annotation { "Feature Type Name" : "Feature", "Feature Type Description" : "" }
export const myFeature = defineFeature(function(context is Context, id is Id, definition is map)
    precondition{}
    {
        {
            var Q0;
            Q0=qCreatedBy(makeId("Top.planeOp"),FACE);
            var sketch = newSketch(context, id + "F0", { "sketchPlane" : qUnion([Q0])});
            skLineSegment(sketch, "E0.bottom", {"start": v(-65, 37.5) * mm, "end": v(-10, 37.5) * mm});
            skLineSegment(sketch, "E0.top", {"start": v(-65, -37.5) * mm, "end": v(-10, -37.5) * mm});
            skLineSegment(sketch, "E0.left", {"start": v(-65, 37.5) * mm, "end": v(-65, -37.5) * mm});
            skLineSegment(sketch, "E0.right", {"start": v(65, 37.5) * mm, "end": v(65, -37.5) * mm});
            skLineSegment(sketch, "E1.bottom", {"start": v(7.7, 29) * mm, "end": v(8.3, 29) * mm});
            skLineSegment(sketch, "E1.top", {"start": v(7.7, -29) * mm, "end": v(8.3, -29) * mm});
            skLineSegment(sketch, "E1.left", {"start": v(7.7, 29) * mm, "end": v(7.7, -29) * mm});
            skLineSegment(sketch, "E1.right", {"start": v(8.3, 29) * mm, "end": v(8.3, -29) * mm});
            skLineSegment(sketch, "E2", {"start": v(8, 29) * mm, "end": v(8, -29) * mm, "construction": true});
            skLineSegment(sketch, "E3.bottom", {"start": v(-46.3, 29) * mm, "end": v(-45.7, 29) * mm});
            skLineSegment(sketch, "E3.top", {"start": v(-46.3, -29) * mm, "end": v(-45.7, -29) * mm});
            skLineSegment(sketch, "E3.left", {"start": v(-46.3, 29) * mm, "end": v(-46.3, -29) * mm});
            skLineSegment(sketch, "E3.right", {"start": v(-45.7, 29) * mm, "end": v(-45.7, -29) * mm});
            skLineSegment(sketch, "E4", {"start": v(-46, -29) * mm, "end": v(-46, 29) * mm, "construction": true});
            skLineSegment(sketch, "E5.bottom", {"start": v(-25, 10) * mm, "end": v(-13, 10) * mm});
            skLineSegment(sketch, "E5.top", {"start": v(-25, -10) * mm, "end": v(-13, -10) * mm});
            skLineSegment(sketch, "E5.left", {"start": v(-25, 10) * mm, "end": v(-25, -10) * mm});
            skLineSegment(sketch, "E5.right", {"start": v(-13, 10) * mm, "end": v(-13, -10) * mm});
            skLineSegment(sketch, "E6", {"start": v(-19, 10) * mm, "end": v(-19, -10) * mm, "construction": true});
            skLineSegment(sketch, "E7.bottom", {"start": v(-8, -35) * mm, "end": v(8, -35) * mm});
            skLineSegment(sketch, "E7.left", {"start": v(-10, -37) * mm, "end": v(-10, -37.5) * mm});
            skLineSegment(sketch, "E7.right", {"start": v(10, -37) * mm, "end": v(10, -37.5) * mm});
            skLineSegment(sketch, "E8.trimOffspring", {"start": v(10, -37.5) * mm, "end": v(65, -37.5) * mm});
            skLineSegment(sketch, "E9.top", {"start": v(-8, 35) * mm, "end": v(8, 35) * mm});
            skLineSegment(sketch, "E9.left", {"start": v(-10, 37.5) * mm, "end": v(-10, 37) * mm});
            skLineSegment(sketch, "E9.right", {"start": v(10, 37.5) * mm, "end": v(10, 37) * mm});
            skLineSegment(sketch, "E10.trimOffspring", {"start": v(10, 37.5) * mm, "end": v(65, 37.5) * mm});
            skPoint(sketch, "E11.visualSharp", {"position": v(-10, 35) * mm});
            skArc(sketch, "E11.filletArc", {"start": v(-10, 37) * mm, "mid": v(-9.41, 35.59) * mm, "end": v(-8, 35) * mm});
            skPoint(sketch, "E12.visualSharp", {"position": v(10, 35) * mm});
            skArc(sketch, "E12.filletArc", {"start": v(8, 35) * mm, "mid": v(9.41, 35.59) * mm, "end": v(10, 37) * mm});
            skPoint(sketch, "E13.visualSharp", {"position": v(-10, -35) * mm});
            skArc(sketch, "E13.filletArc", {"start": v(-8, -35) * mm, "mid": v(-9.41, -35.59) * mm, "end": v(-10, -37) * mm});
            skPoint(sketch, "E14.visualSharp", {"position": v(10, -35) * mm});
            skArc(sketch, "E14.filletArc", {"start": v(10, -37) * mm, "mid": v(9.41, -35.59) * mm, "end": v(8, -35) * mm});
            skSolve(sketch);
        }
        {
            var Q0;
            Q0 = qSketchRegion(id + "F0", true);
            extrude(context, id + "F1", {"entities" : qUnion([Q0]), "depth" : 4 * mm});
        }
        {
            var Q0;
            Q0=makeQuery(id+"F1.opExtrude","CAP_FACE",FACE,{"disambiguationData":[OSD([sQuery(id+"F0.wireOp",EDGE,"E0.bottom"),sQuery(id+"F0.wireOp",EDGE,"E0.top"),sQuery(id+"F0.wireOp",EDGE,"E0.left"),sQuery(id+"F0.wireOp",EDGE,"E0.right"),sQuery(id+"F0.wireOp",EDGE,"E1.bottom"),sQuery(id+"F0.wireOp",EDGE,"E1.top"),sQuery(id+"F0.wireOp",EDGE,"E1.left"),sQuery(id+"F0.wireOp",EDGE,"E1.right"),sQuery(id+"F0.wireOp",EDGE,"E3.bottom"),sQuery(id+"F0.wireOp",EDGE,"E3.top"),sQuery(id+"F0.wireOp",EDGE,"E3.left"),sQuery(id+"F0.wireOp",EDGE,"E3.right")])],"isStart":false});
            var sketch = newSketch(context, id + "F2", { "sketchPlane" : qUnion([Q0])});
            skCircle(sketch, "E15", {"center": v(-35, 11.75) * mm, "radius": 2.5 * mm});
            skCircle(sketch, "E16", {"center": v(-1, 11.75) * mm, "radius": 2.5 * mm});
            skCircle(sketch, "E17", {"center": v(17, 11.75) * mm, "radius": 2.5 * mm});
            skCircle(sketch, "E18", {"center": v(51, 11.75) * mm, "radius": 2.5 * mm});
            skLineSegment(sketch, "E19", {"start": v(8, 29) * mm, "end": v(8, 11.1) * mm, "construction": true});
            skCircle(sketch, "E20.MirrorC", {"center": v(-35, -11.75) * mm, "radius": 2.5 * mm});
            skCircle(sketch, "E21.MirrorC", {"center": v(-1, -11.75) * mm, "radius": 2.5 * mm});
            skCircle(sketch, "E22.MirrorC", {"center": v(17, -11.75) * mm, "radius": 2.5 * mm});
            skCircle(sketch, "E23.MirrorC", {"center": v(51, -11.75) * mm, "radius": 2.5 * mm});
            skLineSegment(sketch, "E24.bottom", {"start": v(65, 37.5) * mm, "end": v(62, 37.5) * mm});
            skLineSegment(sketch, "E24.top", {"start": v(65, -37.5) * mm, "end": v(62, -37.5) * mm});
            skLineSegment(sketch, "E24.left", {"start": v(65, 37.5) * mm, "end": v(65, -37.5) * mm});
            skLineSegment(sketch, "E24.right", {"start": v(62, 37.5) * mm, "end": v(62, -37.5) * mm});
            skSolve(sketch);
        }
        {
            var Q0;
            Q0 = qSketchRegion(id + "F2", true);
            extrude(context, id + "F3", {"entities" : qUnion([Q0]), "operationType" : NewBodyOperationType.ADD, "depth" : 6 * mm});
        }
        {
            var Q0;
            Q0=makeQuery(id+"F1.opExtrude","CAP_FACE",FACE,{"disambiguationData":[OSD([sQuery(id+"F0.wireOp",EDGE,"E0.bottom"),sQuery(id+"F0.wireOp",EDGE,"E0.top"),sQuery(id+"F0.wireOp",EDGE,"E0.left"),sQuery(id+"F0.wireOp",EDGE,"E0.right"),sQuery(id+"F0.wireOp",EDGE,"E1.bottom"),sQuery(id+"F0.wireOp",EDGE,"E1.top"),sQuery(id+"F0.wireOp",EDGE,"E1.left"),sQuery(id+"F0.wireOp",EDGE,"E1.right"),sQuery(id+"F0.wireOp",EDGE,"E3.bottom"),sQuery(id+"F0.wireOp",EDGE,"E3.top"),sQuery(id+"F0.wireOp",EDGE,"E3.left"),sQuery(id+"F0.wireOp",EDGE,"E3.right"),sQuery(id+"F0.wireOp",EDGE,"E5.bottom"),sQuery(id+"F0.wireOp",EDGE,"E5.top"),sQuery(id+"F0.wireOp",EDGE,"E5.left"),sQuery(id+"F0.wireOp",EDGE,"E5.right")])],"isStart":false});
            var sketch = newSketch(context, id + "F4", { "sketchPlane" : qUnion([Q0])});
            skLineSegment(sketch, "E25.bottom", {"start": v(-19.4, 10) * mm, "end": v(-18.6, 10) * mm});
            skLineSegment(sketch, "E25.top", {"start": v(-19.4, 15) * mm, "end": v(-18.6, 15) * mm});
            skLineSegment(sketch, "E25.left", {"start": v(-19.4, 10) * mm, "end": v(-19.4, 15) * mm});
            skLineSegment(sketch, "E25.right", {"start": v(-18.6, 10) * mm, "end": v(-18.6, 15) * mm});
            skLineSegment(sketch, "E26.bottom", {"start": v(-19.4, -10) * mm, "end": v(-18.6, -10) * mm});
            skLineSegment(sketch, "E26.top", {"start": v(-19.4, -15) * mm, "end": v(-18.6, -15) * mm});
            skLineSegment(sketch, "E26.left", {"start": v(-19.4, -10) * mm, "end": v(-19.4, -15) * mm});
            skLineSegment(sketch, "E26.right", {"start": v(-18.6, -10) * mm, "end": v(-18.6, -15) * mm});
            skLineSegment(sketch, "E27", {"start": v(-19, -10) * mm, "end": v(-19, 10) * mm, "construction": true});
            skSolve(sketch);
        }
        {
            var Q0;
            Q0 = qSketchRegion(id + "F4", true);
            extrude(context, id + "F5", {"entities" : qUnion([Q0]), "operationType" : NewBodyOperationType.REMOVE, "oppositeDirection" : true, "depth" : .6 * mm});
        }
        {
            var Q0;
            Q0=makeQuery(id+"F1.opExtrude","CAP_FACE",FACE,{"disambiguationData":[OSD([sQuery(id+"F0.wireOp",EDGE,"E0.bottom"),sQuery(id+"F0.wireOp",EDGE,"E0.top"),sQuery(id+"F0.wireOp",EDGE,"E0.left"),sQuery(id+"F0.wireOp",EDGE,"E0.right"),sQuery(id+"F0.wireOp",EDGE,"E1.bottom"),sQuery(id+"F0.wireOp",EDGE,"E1.top"),sQuery(id+"F0.wireOp",EDGE,"E1.left"),sQuery(id+"F0.wireOp",EDGE,"E1.right"),sQuery(id+"F0.wireOp",EDGE,"E3.bottom"),sQuery(id+"F0.wireOp",EDGE,"E3.top"),sQuery(id+"F0.wireOp",EDGE,"E3.left"),sQuery(id+"F0.wireOp",EDGE,"E3.right"),sQuery(id+"F0.wireOp",EDGE,"E5.bottom"),sQuery(id+"F0.wireOp",EDGE,"E5.top"),sQuery(id+"F0.wireOp",EDGE,"E5.left"),sQuery(id+"F0.wireOp",EDGE,"E5.right")])],"isStart":false});
            var sketch = newSketch(context, id + "F6", { "sketchPlane" : qUnion([Q0])});
            skLineSegment(sketch, "E28.bottom", {"start": v(-65, 37.5) * mm, "end": v(60.6, 37.5) * mm});
            skLineSegment(sketch, "E28.top", {"start": v(-65, -37.5) * mm, "end": v(60.6, -37.5) * mm});
            skLineSegment(sketch, "E28.left", {"start": v(-65, 37.5) * mm, "end": v(-65, -37.5) * mm});
            skLineSegment(sketch, "E28.right", {"start": v(60.6, 37.5) * mm, "end": v(60.6, -37.5) * mm});
            skCircle(sketch, "E29", {"center": v(-35, 11.75) * mm, "radius": 3 * mm});
            skCircle(sketch, "E30", {"center": v(-1, 11.75) * mm, "radius": 3 * mm});
            skCircle(sketch, "E31", {"center": v(17, 11.75) * mm, "radius": 3 * mm});
            skCircle(sketch, "E32", {"center": v(51, 11.75) * mm, "radius": 3 * mm});
            skCircle(sketch, "E33", {"center": v(-35, -11.75) * mm, "radius": 3 * mm});
            skCircle(sketch, "E34", {"center": v(-1, -11.75) * mm, "radius": 3 * mm});
            skCircle(sketch, "E35", {"center": v(17, -11.75) * mm, "radius": 3 * mm});
            skCircle(sketch, "E36", {"center": v(51, -11.75) * mm, "radius": 3 * mm});
            skLineSegment(sketch, "E37.bottom", {"start": v(-46, 29) * mm, "end": v(-46, 29) * mm});
            skLineSegment(sketch, "E37.top", {"start": v(-46, -29) * mm, "end": v(-46, -29) * mm});
            skLineSegment(sketch, "E37.left", {"start": v(-46.4, 28.6) * mm, "end": v(-46.4, -28.6) * mm});
            skLineSegment(sketch, "E37.right", {"start": v(-45.6, 28.6) * mm, "end": v(-45.6, -28.6) * mm});
            skLineSegment(sketch, "E38", {"start": v(-46, 29) * mm, "end": v(-46, 25.94) * mm, "construction": true});
            skLineSegment(sketch, "E39.bottom", {"start": v(8, 29) * mm, "end": v(8, 29) * mm});
            skLineSegment(sketch, "E39.top", {"start": v(8, -29) * mm, "end": v(8, -29) * mm});
            skLineSegment(sketch, "E39.left", {"start": v(7.6, 28.6) * mm, "end": v(7.6, -28.6) * mm});
            skLineSegment(sketch, "E39.right", {"start": v(8.4, 28.6) * mm, "end": v(8.4, -28.6) * mm});
            skLineSegment(sketch, "E40", {"start": v(8, 29) * mm, "end": v(8, 25.9) * mm, "construction": true});
            skLineSegment(sketch, "E41.bottom", {"start": v(-23, 15) * mm, "end": v(-15, 15) * mm});
            skLineSegment(sketch, "E41.top", {"start": v(-23, -15) * mm, "end": v(-15, -15) * mm});
            skLineSegment(sketch, "E41.left", {"start": v(-25, 13) * mm, "end": v(-25, -13) * mm});
            skLineSegment(sketch, "E41.right", {"start": v(-13, 13) * mm, "end": v(-13, -13) * mm});
            skPoint(sketch, "E42.visualSharp", {"position": v(-25, 15) * mm});
            skArc(sketch, "E42.filletArc", {"start": v(-23, 15) * mm, "mid": v(-24.41, 14.41) * mm, "end": v(-25, 13) * mm});
            skPoint(sketch, "E43.visualSharp", {"position": v(-13, 15) * mm});
            skArc(sketch, "E43.filletArc", {"start": v(-13, 13) * mm, "mid": v(-13.59, 14.41) * mm, "end": v(-15, 15) * mm});
            skPoint(sketch, "E44.visualSharp", {"position": v(-13, -15) * mm});
            skArc(sketch, "E44.filletArc", {"start": v(-15, -15) * mm, "mid": v(-13.59, -14.41) * mm, "end": v(-13, -13) * mm});
            skPoint(sketch, "E45.visualSharp", {"position": v(-25, -15) * mm});
            skArc(sketch, "E45.filletArc", {"start": v(-25, -13) * mm, "mid": v(-24.41, -14.41) * mm, "end": v(-23, -15) * mm});
            skPoint(sketch, "E46.visualSharp", {"position": v(-46.4, 29) * mm});
            skArc(sketch, "E46.filletArc", {"start": v(-46, 29) * mm, "mid": v(-46.28, 28.88) * mm, "end": v(-46.4, 28.6) * mm});
            skPoint(sketch, "E47.visualSharp", {"position": v(-45.6, 29) * mm});
            skArc(sketch, "E47.filletArc", {"start": v(-45.6, 28.6) * mm, "mid": v(-45.72, 28.88) * mm, "end": v(-46, 29) * mm});
            skPoint(sketch, "E48.visualSharp", {"position": v(-46.4, -29) * mm});
            skArc(sketch, "E48.filletArc", {"start": v(-46.4, -28.6) * mm, "mid": v(-46.28, -28.88) * mm, "end": v(-46, -29) * mm});
            skPoint(sketch, "E49.visualSharp", {"position": v(-45.6, -29) * mm});
            skArc(sketch, "E49.filletArc", {"start": v(-46, -29) * mm, "mid": v(-45.72, -28.88) * mm, "end": v(-45.6, -28.6) * mm});
            skPoint(sketch, "E50.visualSharp", {"position": v(7.6, 29) * mm});
            skArc(sketch, "E50.filletArc", {"start": v(8, 29) * mm, "mid": v(7.72, 28.88) * mm, "end": v(7.6, 28.6) * mm});
            skPoint(sketch, "E51.visualSharp", {"position": v(8.4, 29) * mm});
            skArc(sketch, "E51.filletArc", {"start": v(8.4, 28.6) * mm, "mid": v(8.28, 28.88) * mm, "end": v(8, 29) * mm});
            skPoint(sketch, "E52.visualSharp", {"position": v(7.6, -29) * mm});
            skArc(sketch, "E52.filletArc", {"start": v(7.6, -28.6) * mm, "mid": v(7.72, -28.88) * mm, "end": v(8, -29) * mm});
            skPoint(sketch, "E53.visualSharp", {"position": v(8.4, -29) * mm});
            skArc(sketch, "E53.filletArc", {"start": v(8, -29) * mm, "mid": v(8.28, -28.88) * mm, "end": v(8.4, -28.6) * mm});
            skSolve(sketch);
        }
        {
            var Q0;
            Q0 = qSketchRegion(id + "F6", true);
            extrude(context, id + "F7", {"entities" : qUnion([Q0]), "depth" : 4 * mm});
        }
        {
            var Q0;
            Q0=makeQuery(id+"F1.opExtrude","SWEPT_EDGE",EDGE,{"disambiguationData":[OSD([sQuery(id+"F0.wireOp",EDGE,"E5.bottom"),sQuery(id+"F0.wireOp",EDGE,"E5.left")])]});
            var Q1;
            Q1=makeQuery(id+"F1.opExtrude","SWEPT_EDGE",EDGE,{"disambiguationData":[OSD([sQuery(id+"F0.wireOp",EDGE,"E5.bottom"),sQuery(id+"F0.wireOp",EDGE,"E5.right")])]});
            var Q2;
            Q2=makeQuery(id+"F1.opExtrude","SWEPT_EDGE",EDGE,{"disambiguationData":[OSD([sQuery(id+"F0.wireOp",EDGE,"E5.top"),sQuery(id+"F0.wireOp",EDGE,"E5.right")])]});
            var Q3;
            Q3=makeQuery(id+"F1.opExtrude","SWEPT_EDGE",EDGE,{"disambiguationData":[OSD([sQuery(id+"F0.wireOp",EDGE,"E5.top"),sQuery(id+"F0.wireOp",EDGE,"E5.left")])]});
            fillet(context, id + "F8", {"entities" : qUnion([Q0, Q1, Q2, Q3]), "radius" : 2 * mm, "tangentPropagation" : true, "allowEdgeOverflow" : false});
        }
        {
            var Q0;
            Q0=makeQuery(id+"F3.opExtrude","CAP_EDGE",EDGE,{"disambiguationData":[OSD([sQuery(id+"F2.wireOp",EDGE,"E15")])],"isStart":false});
            var Q1;
            Q1=makeQuery(id+"F3.opExtrude","CAP_EDGE",EDGE,{"disambiguationData":[OSD([sQuery(id+"F2.wireOp",EDGE,"E20.MirrorC")])],"isStart":false});
            var Q2;
            Q2=makeQuery(id+"F3.opExtrude","CAP_EDGE",EDGE,{"disambiguationData":[OSD([sQuery(id+"F2.wireOp",EDGE,"E16")])],"isStart":false});
            var Q3;
            Q3=makeQuery(id+"F3.opExtrude","CAP_EDGE",EDGE,{"disambiguationData":[OSD([sQuery(id+"F2.wireOp",EDGE,"E21.MirrorC")])],"isStart":false});
            var Q4;
            Q4=makeQuery(id+"F3.opExtrude","CAP_EDGE",EDGE,{"disambiguationData":[OSD([sQuery(id+"F2.wireOp",EDGE,"E17")])],"isStart":false});
            var Q5;
            Q5=makeQuery(id+"F3.opExtrude","CAP_EDGE",EDGE,{"disambiguationData":[OSD([sQuery(id+"F2.wireOp",EDGE,"E22.MirrorC")])],"isStart":false});
            var Q6;
            Q6=makeQuery(id+"F3.opExtrude","CAP_EDGE",EDGE,{"disambiguationData":[OSD([sQuery(id+"F2.wireOp",EDGE,"E18")])],"isStart":false});
            var Q7;
            Q7=makeQuery(id+"F3.opExtrude","CAP_EDGE",EDGE,{"disambiguationData":[OSD([sQuery(id+"F2.wireOp",EDGE,"E23.MirrorC")])],"isStart":false});
            fillet(context, id + "F9", {"entities" : qUnion([Q0, Q1, Q2, Q3, Q4, Q5, Q6, Q7]), "radius" : 1 * mm, "tangentPropagation" : true, "allowEdgeOverflow" : false});
        }
        {
            var Q0;
            Q0=makeQuery(id+"F7.opExtrude","SWEPT_EDGE",EDGE,{"disambiguationData":[OSD([sQuery(id+"F0.wireOp",EDGE,"E8.trimOffspring"),sQuery(id+"F6.wireOp",EDGE,"E28.top"),sQuery(id+"F6.wireOp",EDGE,"E28.right")])]});
            var Q1;
            Q1=makeQuery(id+"F1.opExtrude","SWEPT_EDGE",EDGE,{"disambiguationData":[OSD([sQuery(id+"F0.wireOp",EDGE,"E0.top"),sQuery(id+"F0.wireOp",EDGE,"E0.left")])]});
            var Q2;
            Q2=makeQuery(id+"F1.opExtrude","SWEPT_EDGE",EDGE,{"disambiguationData":[OSD([sQuery(id+"F0.wireOp",EDGE,"E0.bottom"),sQuery(id+"F0.wireOp",EDGE,"E0.left")])]});
            var Q3;
            Q3=makeQuery(id+"F7.opExtrude","SWEPT_EDGE",EDGE,{"disambiguationData":[OSD([sQuery(id+"F6.wireOp",EDGE,"E28.bottom"),sQuery(id+"F6.wireOp",EDGE,"E28.left")])]});
            var Q4;
            Q4=makeQuery(id+"F7.opExtrude","SWEPT_EDGE",EDGE,{"disambiguationData":[OSD([sQuery(id+"F0.wireOp",EDGE,"E10.trimOffspring"),sQuery(id+"F6.wireOp",EDGE,"E28.bottom"),sQuery(id+"F6.wireOp",EDGE,"E28.right")])]});
            var Q5;
            Q5=makeQuery(id+"F7.opExtrude","SWEPT_EDGE",EDGE,{"disambiguationData":[OSD([sQuery(id+"F6.wireOp",EDGE,"E28.top"),sQuery(id+"F6.wireOp",EDGE,"E28.left")])]});
            var Q6;
            Q6=makeQuery(id+"F1.opExtrude","SWEPT_EDGE",EDGE,{"disambiguationData":[OSD([sQuery(id+"F0.wireOp",EDGE,"E0.top"),sQuery(id+"F0.wireOp",EDGE,"E7.left")])]});
            var Q7;
            Q7=makeQuery(id+"F1.opExtrude","SWEPT_EDGE",EDGE,{"disambiguationData":[OSD([sQuery(id+"F0.wireOp",EDGE,"E9.right"),sQuery(id+"F0.wireOp",EDGE,"E10.trimOffspring")])]});
            var Q8;
            Q8=makeQuery(id+"F1.opExtrude","SWEPT_EDGE",EDGE,{"disambiguationData":[OSD([sQuery(id+"F0.wireOp",EDGE,"E0.bottom"),sQuery(id+"F0.wireOp",EDGE,"E9.left")])]});
            var Q9;
            Q9=makeQuery(id+"F3.opExtrude","CAP_EDGE",EDGE,{"disambiguationData":[OSD([sQuery(id+"F2.wireOp",EDGE,"E24.bottom")])],"isStart":false});
            var Q10;
            Q10=makeQuery(id+"F3.opExtrude","CAP_EDGE",EDGE,{"disambiguationData":[OSD([sQuery(id+"F2.wireOp",EDGE,"E24.top")])],"isStart":false});
            var Q11;
            Q11=makeQuery(id+"F1.opExtrude","SWEPT_EDGE",EDGE,{"disambiguationData":[OSD([sQuery(id+"F0.wireOp",EDGE,"E7.right"),sQuery(id+"F0.wireOp",EDGE,"E8.trimOffspring")])]});
            fillet(context, id + "F10", {"entities" : qUnion([Q0, Q1, Q2, Q3, Q4, Q5, Q6, Q7, Q8, Q9, Q10, Q11]), "radius" : 5 * mm, "tangentPropagation" : true, "allowEdgeOverflow" : false});
        }
        {
            var Q0;
            Q0=makeQuery(id+"F1.opExtrude","CAP_FACE",FACE,{"disambiguationData":[OSD([sQuery(id+"F0.wireOp",EDGE,"E0.bottom"),sQuery(id+"F0.wireOp",EDGE,"E0.top"),sQuery(id+"F0.wireOp",EDGE,"E0.left"),sQuery(id+"F0.wireOp",EDGE,"E0.right"),sQuery(id+"F0.wireOp",EDGE,"E1.bottom"),sQuery(id+"F0.wireOp",EDGE,"E1.top"),sQuery(id+"F0.wireOp",EDGE,"E1.left"),sQuery(id+"F0.wireOp",EDGE,"E1.right"),sQuery(id+"F0.wireOp",EDGE,"E3.bottom"),sQuery(id+"F0.wireOp",EDGE,"E3.top"),sQuery(id+"F0.wireOp",EDGE,"E3.left"),sQuery(id+"F0.wireOp",EDGE,"E3.right"),sQuery(id+"F0.wireOp",EDGE,"E5.bottom"),sQuery(id+"F0.wireOp",EDGE,"E5.top"),sQuery(id+"F0.wireOp",EDGE,"E5.left"),sQuery(id+"F0.wireOp",EDGE,"E5.right"),sQuery(id+"F0.wireOp",EDGE,"E7.bottom"),sQuery(id+"F0.wireOp",EDGE,"E7.left"),sQuery(id+"F0.wireOp",EDGE,"E7.right"),sQuery(id+"F0.wireOp",EDGE,"E8.trimOffspring"),sQuery(id+"F0.wireOp",EDGE,"E9.top"),sQuery(id+"F0.wireOp",EDGE,"E9.left"),sQuery(id+"F0.wireOp",EDGE,"E9.right"),sQuery(id+"F0.wireOp",EDGE,"E10.trimOffspring"),sQuery(id+"F0.wireOp",EDGE,"E11.filletArc"),sQuery(id+"F0.wireOp",EDGE,"E12.filletArc"),sQuery(id+"F0.wireOp",EDGE,"E13.filletArc"),sQuery(id+"F0.wireOp",EDGE,"E14.filletArc")])],"isStart":true});
            fillet(context, id + "F11", {"entities" : qUnion([Q0]), "radius" : .75 * mm, "tangentPropagation" : true, "allowEdgeOverflow" : false});
        }
        {
            var Q0;
            Q0=makeQuery(id+"F7.opExtrude","CAP_FACE",FACE,{"disambiguationData":[OSD([sQuery(id+"F6.wireOp",EDGE,"E28.bottom"),sQuery(id+"F6.wireOp",EDGE,"E28.top"),sQuery(id+"F6.wireOp",EDGE,"E28.left"),sQuery(id+"F6.wireOp",EDGE,"E28.right"),sQuery(id+"F6.wireOp",EDGE,"E29"),sQuery(id+"F6.wireOp",EDGE,"E30"),sQuery(id+"F6.wireOp",EDGE,"E31"),sQuery(id+"F6.wireOp",EDGE,"E32"),sQuery(id+"F6.wireOp",EDGE,"E33"),sQuery(id+"F6.wireOp",EDGE,"E34"),sQuery(id+"F6.wireOp",EDGE,"E35"),sQuery(id+"F6.wireOp",EDGE,"E36"),sQuery(id+"F6.wireOp",EDGE,"E37.left"),sQuery(id+"F6.wireOp",EDGE,"E37.right"),sQuery(id+"F6.wireOp",EDGE,"E39.left"),sQuery(id+"F6.wireOp",EDGE,"E39.right"),sQuery(id+"F6.wireOp",EDGE,"E41.bottom"),sQuery(id+"F6.wireOp",EDGE,"E41.top"),sQuery(id+"F6.wireOp",EDGE,"E41.left"),sQuery(id+"F6.wireOp",EDGE,"E41.right"),sQuery(id+"F6.wireOp",EDGE,"E42.filletArc"),sQuery(id+"F6.wireOp",EDGE,"E43.filletArc"),sQuery(id+"F6.wireOp",EDGE,"E44.filletArc"),sQuery(id+"F6.wireOp",EDGE,"E45.filletArc"),sQuery(id+"F6.wireOp",EDGE,"E46.filletArc"),sQuery(id+"F6.wireOp",EDGE,"E47.filletArc"),sQuery(id+"F6.wireOp",EDGE,"E48.filletArc"),sQuery(id+"F6.wireOp",EDGE,"E49.filletArc"),sQuery(id+"F6.wireOp",EDGE,"E50.filletArc"),sQuery(id+"F6.wireOp",EDGE,"E51.filletArc"),sQuery(id+"F6.wireOp",EDGE,"E52.filletArc"),sQuery(id+"F6.wireOp",EDGE,"E53.filletArc")])],"isStart":true});
            fillet(context, id + "F12", {"entities" : qUnion([Q0]), "radius" : .75 * mm, "tangentPropagation" : true, "allowEdgeOverflow" : false});
        }
        {
            var Q0;
            Q0=makeQuery(id+"F1.opExtrude","CAP_FACE",FACE,{"disambiguationData":[OSD([sQuery(id+"F0.wireOp",EDGE,"E0.bottom"),sQuery(id+"F0.wireOp",EDGE,"E0.top"),sQuery(id+"F0.wireOp",EDGE,"E0.left"),sQuery(id+"F0.wireOp",EDGE,"E0.right"),sQuery(id+"F0.wireOp",EDGE,"E1.bottom"),sQuery(id+"F0.wireOp",EDGE,"E1.top"),sQuery(id+"F0.wireOp",EDGE,"E1.left"),sQuery(id+"F0.wireOp",EDGE,"E1.right"),sQuery(id+"F0.wireOp",EDGE,"E3.bottom"),sQuery(id+"F0.wireOp",EDGE,"E3.top"),sQuery(id+"F0.wireOp",EDGE,"E3.left"),sQuery(id+"F0.wireOp",EDGE,"E3.right"),sQuery(id+"F0.wireOp",EDGE,"E5.bottom"),sQuery(id+"F0.wireOp",EDGE,"E5.top"),sQuery(id+"F0.wireOp",EDGE,"E5.left"),sQuery(id+"F0.wireOp",EDGE,"E5.right"),sQuery(id+"F0.wireOp",EDGE,"E7.bottom"),sQuery(id+"F0.wireOp",EDGE,"E7.left"),sQuery(id+"F0.wireOp",EDGE,"E7.right"),sQuery(id+"F0.wireOp",EDGE,"E8.trimOffspring"),sQuery(id+"F0.wireOp",EDGE,"E9.top"),sQuery(id+"F0.wireOp",EDGE,"E9.left"),sQuery(id+"F0.wireOp",EDGE,"E9.right"),sQuery(id+"F0.wireOp",EDGE,"E10.trimOffspring"),sQuery(id+"F0.wireOp",EDGE,"E11.filletArc"),sQuery(id+"F0.wireOp",EDGE,"E12.filletArc"),sQuery(id+"F0.wireOp",EDGE,"E13.filletArc"),sQuery(id+"F0.wireOp",EDGE,"E14.filletArc")])],"isStart":false});
            var sketch = newSketch(context, id + "F13", { "sketchPlane" : qUnion([Q0])});
            skLineSegment(sketch, "E54.bottom", {"start": v(62, 13.94) * mm, "end": v(60, 13.94) * mm});
            skLineSegment(sketch, "E54.top", {"start": v(62, -13.94) * mm, "end": v(60, -13.94) * mm});
            skLineSegment(sketch, "E54.left", {"start": v(62, 13.94) * mm, "end": v(62, -13.94) * mm});
            skLineSegment(sketch, "E54.right", {"start": v(60, 13.94) * mm, "end": v(60, -13.94) * mm});
            skSolve(sketch);
        }
        {
            var Q0;
            Q0 = qSketchRegion(id + "F13", true);
            extrude(context, id + "F14", {"entities" : qUnion([Q0]), "operationType" : NewBodyOperationType.REMOVE, "oppositeDirection" : true, "depth" : 1 * mm});
        }
        {
            var Q0;
            Q0=makeQuery(id+"F1.opExtrude","CAP_FACE",FACE,{"disambiguationData":[OSD([sQuery(id+"F0.wireOp",EDGE,"E0.bottom"),sQuery(id+"F0.wireOp",EDGE,"E0.top"),sQuery(id+"F0.wireOp",EDGE,"E0.left"),sQuery(id+"F0.wireOp",EDGE,"E0.right"),sQuery(id+"F0.wireOp",EDGE,"E1.bottom"),sQuery(id+"F0.wireOp",EDGE,"E1.top"),sQuery(id+"F0.wireOp",EDGE,"E1.left"),sQuery(id+"F0.wireOp",EDGE,"E1.right"),sQuery(id+"F0.wireOp",EDGE,"E3.bottom"),sQuery(id+"F0.wireOp",EDGE,"E3.top"),sQuery(id+"F0.wireOp",EDGE,"E3.left"),sQuery(id+"F0.wireOp",EDGE,"E3.right"),sQuery(id+"F0.wireOp",EDGE,"E5.bottom"),sQuery(id+"F0.wireOp",EDGE,"E5.top"),sQuery(id+"F0.wireOp",EDGE,"E5.left"),sQuery(id+"F0.wireOp",EDGE,"E5.right"),sQuery(id+"F0.wireOp",EDGE,"E7.bottom"),sQuery(id+"F0.wireOp",EDGE,"E7.left"),sQuery(id+"F0.wireOp",EDGE,"E7.right"),sQuery(id+"F0.wireOp",EDGE,"E8.trimOffspring"),sQuery(id+"F0.wireOp",EDGE,"E9.top"),sQuery(id+"F0.wireOp",EDGE,"E9.left"),sQuery(id+"F0.wireOp",EDGE,"E9.right"),sQuery(id+"F0.wireOp",EDGE,"E10.trimOffspring"),sQuery(id+"F0.wireOp",EDGE,"E11.filletArc"),sQuery(id+"F0.wireOp",EDGE,"E12.filletArc"),sQuery(id+"F0.wireOp",EDGE,"E13.filletArc"),sQuery(id+"F0.wireOp",EDGE,"E14.filletArc")])],"isStart":false});
            var sketch = newSketch(context, id + "F15", { "sketchPlane" : qUnion([Q0])});
            skCircle(sketch, "E55", {"center": v(-35, 11.75) * mm, "radius": 3.25 * mm});
            skCircle(sketch, "E56", {"center": v(-35, 11.75) * mm, "radius": 2.5 * mm});
            skCircle(sketch, "E57", {"center": v(-1, 11.75) * mm, "radius": 3.25 * mm});
            skCircle(sketch, "E58", {"center": v(-1, 11.75) * mm, "radius": 2.5 * mm});
            skCircle(sketch, "E59", {"center": v(17, 11.75) * mm, "radius": 3.25 * mm});
            skCircle(sketch, "E60", {"center": v(17, 11.75) * mm, "radius": 2.5 * mm});
            skCircle(sketch, "E61", {"center": v(51, 11.75) * mm, "radius": 3.25 * mm});
            skCircle(sketch, "E62", {"center": v(51, 11.75) * mm, "radius": 2.5 * mm});
            skCircle(sketch, "E63", {"center": v(-35, -11.75) * mm, "radius": 3.25 * mm});
            skCircle(sketch, "E64", {"center": v(-35, -11.75) * mm, "radius": 2.5 * mm});
            skCircle(sketch, "E65", {"center": v(-1, -11.75) * mm, "radius": 3.25 * mm});
            skCircle(sketch, "E66", {"center": v(-1, -11.75) * mm, "radius": 2.5 * mm});
            skCircle(sketch, "E67", {"center": v(17, -11.75) * mm, "radius": 3.25 * mm});
            skCircle(sketch, "E68", {"center": v(17, -11.75) * mm, "radius": 2.5 * mm});
            skCircle(sketch, "E69", {"center": v(51, -11.75) * mm, "radius": 3.25 * mm});
            skCircle(sketch, "E70", {"center": v(51, -11.75) * mm, "radius": 2.5 * mm});
            skSolve(sketch);
        }
        {
            var Q0;
            Q0 = qSketchRegion(id + "F15", true);
            extrude(context, id + "F16", {"entities" : qUnion([Q0]), "operationType" : NewBodyOperationType.REMOVE, "oppositeDirection" : true, "depth" : .6 * mm});
        }
        {
            var Q0;
            {var subQ0=sQuery(id+"F6.wireOp",EDGE,"E28.right");var subQ1=sQuery(id+"F6.wireOp",EDGE,"E28.bottom");var subQ2=sQuery(id+"F6.wireOp",EDGE,"E28.left");var subQ3=sQuery(id+"F6.wireOp",EDGE,"E28.top");var subQ4=sQuery(id+"F6.wireOp",EDGE,"E53.filletArc");var subQ5=sQuery(id+"F6.wireOp",EDGE,"E52.filletArc");var subQ6=sQuery(id+"F6.wireOp",EDGE,"E51.filletArc");var subQ7=sQuery(id+"F6.wireOp",EDGE,"E50.filletArc");var subQ8=sQuery(id+"F6.wireOp",EDGE,"E49.filletArc");var subQ9=sQuery(id+"F6.wireOp",EDGE,"E48.filletArc");var subQ10=sQuery(id+"F6.wireOp",EDGE,"E47.filletArc");var subQ11=sQuery(id+"F6.wireOp",EDGE,"E46.filletArc");var subQ12=sQuery(id+"F6.wireOp",EDGE,"E45.filletArc");var subQ13=sQuery(id+"F6.wireOp",EDGE,"E44.filletArc");var subQ14=sQuery(id+"F6.wireOp",EDGE,"E41.bottom");var subQ15=sQuery(id+"F6.wireOp",EDGE,"E39.right");var subQ16=sQuery(id+"F6.wireOp",EDGE,"E39.left");var subQ17=sQuery(id+"F6.wireOp",EDGE,"E37.right");var subQ18=sQuery(id+"F6.wireOp",EDGE,"E43.filletArc");var subQ19=sQuery(id+"F6.wireOp",EDGE,"E37.left");var subQ20=sQuery(id+"F6.wireOp",EDGE,"E42.filletArc");var subQ21=sQuery(id+"F6.wireOp",EDGE,"E36");var subQ22=sQuery(id+"F6.wireOp",EDGE,"E41.right");var subQ23=sQuery(id+"F6.wireOp",EDGE,"E35");var subQ24=sQuery(id+"F6.wireOp",EDGE,"E34");var subQ25=sQuery(id+"F6.wireOp",EDGE,"E33");var subQ26=sQuery(id+"F6.wireOp",EDGE,"E32");var subQ27=sQuery(id+"F6.wireOp",EDGE,"E31");var subQ28=sQuery(id+"F6.wireOp",EDGE,"E30");var subQ29=sQuery(id+"F6.wireOp",EDGE,"E29");var subQ30=sQuery(id+"F6.wireOp",EDGE,"E41.top");var subQ31=sQuery(id+"F6.wireOp",EDGE,"E41.left");Q0=makeQuery(id+"F22.boolean.opBoolean","SPLIT",FACE,{"disambiguationData":[TD([makeQuery(id+"F7.opExtrude","SWEPT_FACE",FACE,{"disambiguationData":[OSD([subQ1])]})])],"derivedFrom":makeQuery(id+"F7.opExtrude","CAP_FACE",FACE,{"disambiguationData":[OSD([subQ1,subQ3,subQ2,subQ0,subQ29,subQ28,subQ27,subQ26,subQ25,subQ24,subQ23,subQ21,subQ19,subQ17,subQ16,subQ15,subQ14,subQ30,subQ31,subQ22,subQ20,subQ18,subQ13,subQ12,subQ11,subQ10,subQ9,subQ8,subQ7,subQ6,subQ5,subQ4])],"isStart":false})});}
            var sketch = newSketch(context, id + "F17", { "sketchPlane" : qUnion([Q0])});
            skLineSegment(sketch, "E71.bottom", {"start": v(-49.4, 5) * mm, "end": v(-39.6, 5) * mm});
            skLineSegment(sketch, "E71.top", {"start": v(-49.4, -5) * mm, "end": v(-39.6, -5) * mm});
            skLineSegment(sketch, "E71.right", {"start": v(-39.6, 5) * mm, "end": v(-39.6, -5) * mm});
            skLineSegment(sketch, "E72.bottom", {"start": v(-49.4, 10) * mm, "end": v(-65, 10) * mm});
            skLineSegment(sketch, "E72.top", {"start": v(-49.4, -10) * mm, "end": v(-65, -10) * mm});
            skLineSegment(sketch, "E72.left", {"start": v(-49.4, 10) * mm, "end": v(-49.4, 5) * mm});
            skLineSegment(sketch, "E72.right", {"start": v(-65, 10) * mm, "end": v(-65, -10) * mm});
            skLineSegment(sketch, "E73.trimOffspring", {"start": v(-49.4, -5) * mm, "end": v(-49.4, -10) * mm});
            skSolve(sketch);
        }
        {
            var Q0;
            Q0 = qSketchRegion(id + "F17", true);
            extrude(context, id + "F18", {"entities" : qUnion([Q0]), "operationType" : NewBodyOperationType.REMOVE, "endBound" : BoundingType.THROUGH_ALL, "oppositeDirection" : true, "depth" : 25 * mm});
        }
        {
            var Q0;
            Q0=makeQuery(id+"F18.boolean.opBoolean","COPY",EDGE,{"derivedFrom":makeQuery(id+"F18.opExtrude","SWEPT_EDGE",EDGE,{"disambiguationData":[OSD([sQuery(id+"F17.wireOp",EDGE,"E71.bottom"),sQuery(id+"F17.wireOp",EDGE,"E71.right")])]})});
            var Q1;
            Q1=makeQuery(id+"F18.boolean.opBoolean","COPY",EDGE,{"derivedFrom":makeQuery(id+"F18.opExtrude","SWEPT_EDGE",EDGE,{"disambiguationData":[OSD([sQuery(id+"F17.wireOp",EDGE,"E71.top"),sQuery(id+"F17.wireOp",EDGE,"E71.right")])]})});
            var Q2;
            Q2=makeQuery(id+"F18.boolean.opBoolean","COPY",EDGE,{"derivedFrom":makeQuery(id+"F18.opExtrude","SWEPT_EDGE",EDGE,{"disambiguationData":[OSD([sQuery(id+"F17.wireOp",EDGE,"E71.top"),sQuery(id+"F17.wireOp",EDGE,"E71.left")])]})});
            var Q3;
            Q3=makeQuery(id+"F18.boolean.opBoolean","COPY",EDGE,{"derivedFrom":makeQuery(id+"F18.opExtrude","SWEPT_EDGE",EDGE,{"disambiguationData":[OSD([sQuery(id+"F17.wireOp",EDGE,"E71.bottom"),sQuery(id+"F17.wireOp",EDGE,"E71.left")])]})});
            var Q4;
            Q4=makeQuery(id+"F18.boolean.opBoolean","COPY",EDGE,{"derivedFrom":makeQuery(id+"F18.opExtrude","SWEPT_EDGE",EDGE,{"disambiguationData":[OSD([sQuery(id+"F17.wireOp",EDGE,"E72.bottom"),sQuery(id+"F17.wireOp",EDGE,"E72.left")])]})});
            var Q5;
            Q5=makeQuery(id+"F18.boolean.opBoolean","COPY",EDGE,{"derivedFrom":makeQuery(id+"F18.opExtrude","SWEPT_EDGE",EDGE,{"disambiguationData":[OSD([sQuery(id+"F17.wireOp",EDGE,"E72.top"),sQuery(id+"F17.wireOp",EDGE,"E73.trimOffspring")])]})});
            fillet(context, id + "F19", {"entities" : qUnion([Q0, Q1, Q2, Q3, Q4, Q5]), "radius" : 2 * mm, "tangentPropagation" : true, "allowEdgeOverflow" : false});
        }
        {
            var Q0;
            Q0=makeQuery(id+"F7.opExtrude","CAP_FACE",FACE,{"disambiguationData":[OSD([sQuery(id+"F6.wireOp",EDGE,"E28.bottom"),sQuery(id+"F6.wireOp",EDGE,"E28.top"),sQuery(id+"F6.wireOp",EDGE,"E28.left"),sQuery(id+"F6.wireOp",EDGE,"E28.right"),sQuery(id+"F6.wireOp",EDGE,"E29"),sQuery(id+"F6.wireOp",EDGE,"E30"),sQuery(id+"F6.wireOp",EDGE,"E31"),sQuery(id+"F6.wireOp",EDGE,"E32"),sQuery(id+"F6.wireOp",EDGE,"E33"),sQuery(id+"F6.wireOp",EDGE,"E34"),sQuery(id+"F6.wireOp",EDGE,"E35"),sQuery(id+"F6.wireOp",EDGE,"E36"),sQuery(id+"F6.wireOp",EDGE,"E37.left"),sQuery(id+"F6.wireOp",EDGE,"E37.right"),sQuery(id+"F6.wireOp",EDGE,"E39.left"),sQuery(id+"F6.wireOp",EDGE,"E39.right"),sQuery(id+"F6.wireOp",EDGE,"E41.bottom"),sQuery(id+"F6.wireOp",EDGE,"E41.top"),sQuery(id+"F6.wireOp",EDGE,"E41.left"),sQuery(id+"F6.wireOp",EDGE,"E41.right"),sQuery(id+"F6.wireOp",EDGE,"E42.filletArc"),sQuery(id+"F6.wireOp",EDGE,"E43.filletArc"),sQuery(id+"F6.wireOp",EDGE,"E44.filletArc"),sQuery(id+"F6.wireOp",EDGE,"E45.filletArc"),sQuery(id+"F6.wireOp",EDGE,"E46.filletArc"),sQuery(id+"F6.wireOp",EDGE,"E47.filletArc"),sQuery(id+"F6.wireOp",EDGE,"E48.filletArc"),sQuery(id+"F6.wireOp",EDGE,"E49.filletArc"),sQuery(id+"F6.wireOp",EDGE,"E50.filletArc"),sQuery(id+"F6.wireOp",EDGE,"E51.filletArc"),sQuery(id+"F6.wireOp",EDGE,"E52.filletArc"),sQuery(id+"F6.wireOp",EDGE,"E53.filletArc")])],"isStart":false});
            fillet(context, id + "F20", {"entities" : qUnion([Q0]), "radius" : .75 * mm, "tangentPropagation" : true, "allowEdgeOverflow" : false});
        }
        {
            var Q0;
            Q0=makeQuery(id+"F7.opExtrude","CAP_FACE",FACE,{"disambiguationData":[OSD([sQuery(id+"F6.wireOp",EDGE,"E28.bottom"),sQuery(id+"F6.wireOp",EDGE,"E28.top"),sQuery(id+"F6.wireOp",EDGE,"E28.left"),sQuery(id+"F6.wireOp",EDGE,"E28.right"),sQuery(id+"F6.wireOp",EDGE,"E29"),sQuery(id+"F6.wireOp",EDGE,"E30"),sQuery(id+"F6.wireOp",EDGE,"E31"),sQuery(id+"F6.wireOp",EDGE,"E32"),sQuery(id+"F6.wireOp",EDGE,"E33"),sQuery(id+"F6.wireOp",EDGE,"E34"),sQuery(id+"F6.wireOp",EDGE,"E35"),sQuery(id+"F6.wireOp",EDGE,"E36"),sQuery(id+"F6.wireOp",EDGE,"E37.left"),sQuery(id+"F6.wireOp",EDGE,"E37.right"),sQuery(id+"F6.wireOp",EDGE,"E39.left"),sQuery(id+"F6.wireOp",EDGE,"E39.right"),sQuery(id+"F6.wireOp",EDGE,"E41.bottom"),sQuery(id+"F6.wireOp",EDGE,"E41.top"),sQuery(id+"F6.wireOp",EDGE,"E41.left"),sQuery(id+"F6.wireOp",EDGE,"E41.right"),sQuery(id+"F6.wireOp",EDGE,"E42.filletArc"),sQuery(id+"F6.wireOp",EDGE,"E43.filletArc"),sQuery(id+"F6.wireOp",EDGE,"E44.filletArc"),sQuery(id+"F6.wireOp",EDGE,"E45.filletArc"),sQuery(id+"F6.wireOp",EDGE,"E46.filletArc"),sQuery(id+"F6.wireOp",EDGE,"E47.filletArc"),sQuery(id+"F6.wireOp",EDGE,"E48.filletArc"),sQuery(id+"F6.wireOp",EDGE,"E49.filletArc"),sQuery(id+"F6.wireOp",EDGE,"E50.filletArc"),sQuery(id+"F6.wireOp",EDGE,"E51.filletArc"),sQuery(id+"F6.wireOp",EDGE,"E52.filletArc"),sQuery(id+"F6.wireOp",EDGE,"E53.filletArc")])],"isStart":false});
            var sketch = newSketch(context, id + "F21", { "sketchPlane" : qUnion([Q0])});
            skText(sketch, "E74", { "text": "Phosentix Film Trimmer\nRev A", "fontName": "OpenSans-Regular.ttf"});
            const initialGuessF21  = {"E74": [-0.05991, 0.0308, 1, 0, 0.003]};
            skSetInitialGuess(sketch, initialGuessF21);
            skSolve(sketch);
        }
        {
            var Q0;
            Q0 = qSketchRegion(id + "F21", true);
            extrude(context, id + "F22", {"entities" : qUnion([Q0]), "operationType" : NewBodyOperationType.ADD, "depth" : .5 * mm});
        }
    });